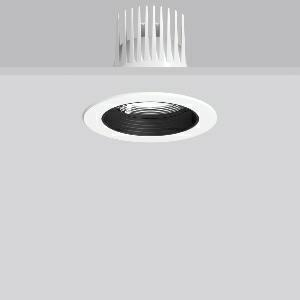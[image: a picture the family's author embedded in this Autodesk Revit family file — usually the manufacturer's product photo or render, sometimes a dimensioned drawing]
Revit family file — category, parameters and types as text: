
# Revit family: heledon_maxi_e_901768_002_2_76_8a79
name_source: partatom
category: Lighting Fixtures
units: mm (PartAtom-declared; Revit-internal decimal feet)

## family parameters
Cut with Voids When Loaded = No
Host = Face
Light Source = No
Part Type = Normal
Room Calculation Point = No
Round Connector Dimension = Use Diameter
Shared = No

## types (1)
- HELEDON maxi E (1 x LED Modul 927, 3350 lm, 2700)
    Apparent Load = 35 VA
    Approval mark = CE
    CIE Flux Codes = 96 100 100 100 100
    Color Rendering = 92
    Color Temperature = 2700
    Default Elevation = 1800 mm
    Description = Series: HELEDON maxi
Round recessed downlight. Housing: die-cast aluminium, powder-coated. Black plastic ring and recessed LED to prevent glare from the side. Optical assembly with lens made of plastic (polycarbonate) for the best homogeneous light distribution - can be changed without tools. Best colour rendering index Ra>90. Suitable for Recessed ceiling mounting. Installation without tools thanks to spring fastening system. Including separate LED converter with connecting cable 600 mm.High quality converter without flickering and stroboscopic effect. Through-wiring box (5 pole) available as accessory. The following accessories can be mounted without use of tools: interchangeable lenses, decorative glasses, honeycomb louvre, clear and frosted diffusers, white interchangeable plastic ring. 
Colour: traffic white, matt (RAL 9016)
Diameter: 162 mm
Height: 3 mm
Cut-out diameter: 152 mm
Recess height: 200 mm
Luminaire: recess height: 135 mm
Lamp: LED
Socket: without socket
Colour temperature: 2700K
Colour rendering index (CRI): 92
System power: 35 W
Rated luminous flux: 3350 lm
Luminous efficiency: 96 lm/W
Control gear: Converter, dimmable, DALI
Protection class: II
Type of protection: IP 20
    Height = 0 mm  [stored 0 ft]
    Lamp = 1 x LED Modul 927
    Lamp Light Flux = 3350 lm
    Lamp count = 1
    Length = 162 mm
    Lifetime = 50000 h
    Luminous efficacy = 96 lm/W
    Manufacturer = RZB
    ModVariant = No
    Model = 901768.002.2.76
    Mounting Place = Ceiling
    Mounting Type = Recessed
    Number of Poles = 1
    OnlyDefault = Yes
    Power Factor = 1
    Product Name = HELEDON maxi E
    Product group = Recessed downlights
    ProductGroupID = 402
    Protection Class = Protection class II
    Protection Degree = IP 20
    RLX_Detail_Level = 1
    RLX_Emergency_Light_Flux = 0 lm
    RLX_Emergency_Type = 0
    RLX_Emergency_Type_DB = No
    RlxData = <blob elided: 118857 chars, md5=8815383f>
    Socket = socket
    Standby Power = 0 W
    System Light Flux = 3350 lm
    System Power = 35 W
    Type Comments = Product without accessories
    Type Image = 901663.002.jpg
    URL = http://relux.com
    VarID = ---
    Voltage = 230 V
    Voltage Range = 220-240 V
    Weight = 0.00 kg
    Width = 0 mm  [stored 0 ft]

note: [stored X ft] marks values corroborated as IEEE doubles in the binary element streams (Revit-internal decimal feet)

## geometry (parser evidence)
native form markers: Blend x4, Sweep x11
no freeform markers — native parametric forms only
